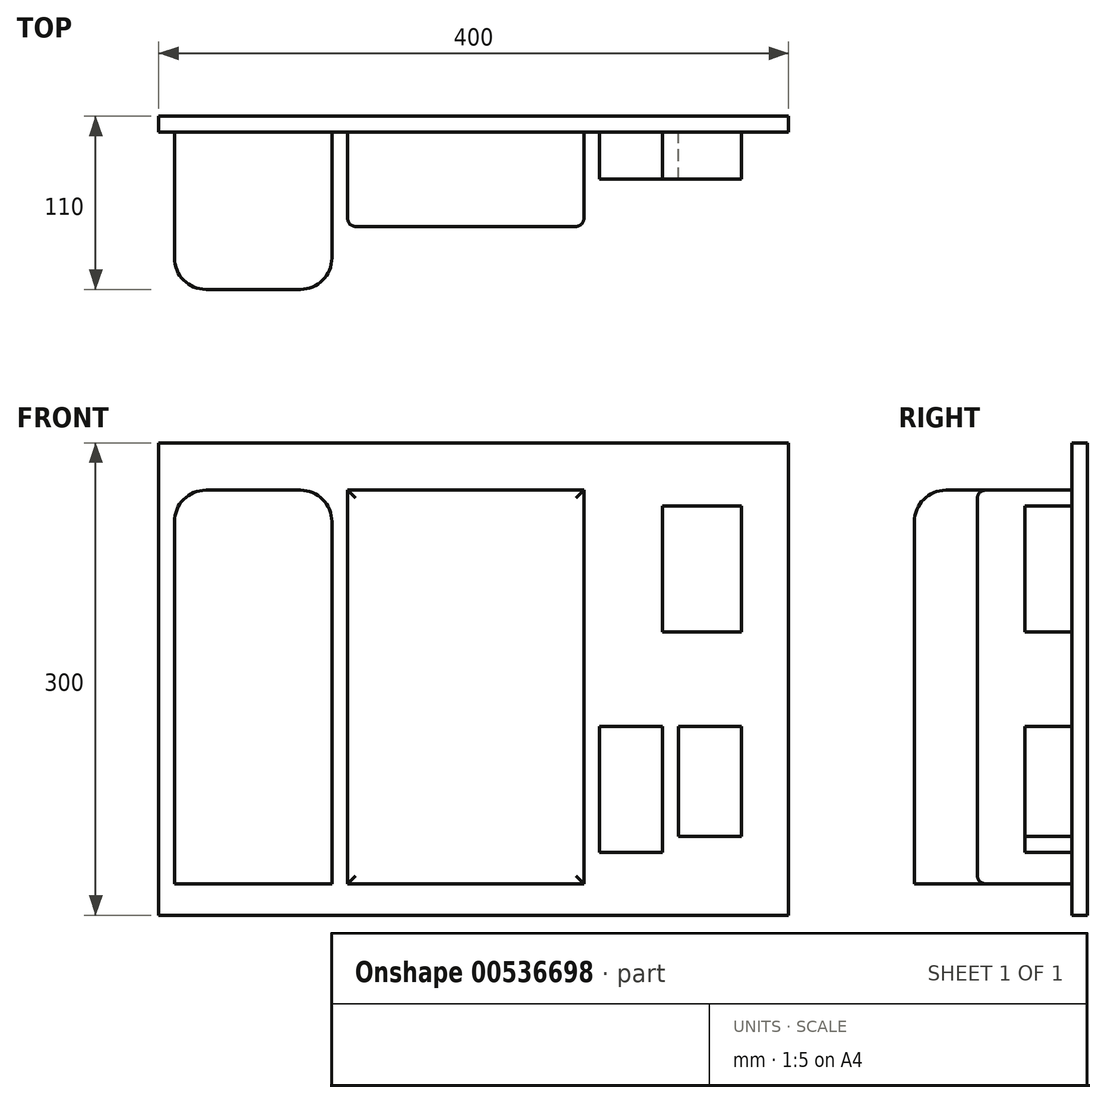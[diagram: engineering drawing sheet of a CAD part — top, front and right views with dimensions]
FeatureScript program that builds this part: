
annotation { "Feature Type Name" : "Feature", "Feature Type Description" : "" }
export const myFeature = defineFeature(function(context is Context, id is Id, definition is map)
    precondition{}
    {
        {
            var Q0;
            Q0=qCreatedBy(makeId("Front.planeOp"),FACE);
            var sketch = newSketch(context, id + "F0", { "sketchPlane" : qUnion([Q0])});
            skLineSegment(sketch, "E0.bottom", {"start": v(-200, 150) * mm, "end": v(200, 150) * mm});
            skLineSegment(sketch, "E0.top", {"start": v(-200, -150) * mm, "end": v(200, -150) * mm});
            skLineSegment(sketch, "E0.left", {"start": v(-200, 150) * mm, "end": v(-200, -150) * mm});
            skLineSegment(sketch, "E0.right", {"start": v(200, 150) * mm, "end": v(200, -150) * mm});
            skSolve(sketch);
        }
        {
            var Q0;
            Q0=makeQuery(id+"F0.imprint","IMPRINT",FACE,{"disambiguationData":[TD([[makeQuery(id+"F0.imprint","IMPRINT",EDGE,{"derivedFrom":sQuery(id+"F0.wireOp",EDGE,"E0.bottom")}),-1.0]])]});
            extrude(context, id + "F1", {"entities" : qUnion([Q0]), "endBound" : BoundingType.SYMMETRIC, "depth" : 10 * mm, "offsetDistance" : 25 * mm});
        }
        {
            var Q0;
            Q0=makeQuery(id+"F1.opExtrude","CAP_FACE",FACE,{"disambiguationData":[OSD([sQuery(id+"F0.wireOp",EDGE,"E0.bottom"),sQuery(id+"F0.wireOp",EDGE,"E0.top"),sQuery(id+"F0.wireOp",EDGE,"E0.left"),sQuery(id+"F0.wireOp",EDGE,"E0.right")])],"isStart":false});
            var sketch = newSketch(context, id + "F2", { "sketchPlane" : qUnion([Q0])});
            skLineSegment(sketch, "E1.bottom", {"start": v(-190, 120) * mm, "end": v(-90, 120) * mm});
            skLineSegment(sketch, "E1.top", {"start": v(-190, -130) * mm, "end": v(-90, -130) * mm});
            skLineSegment(sketch, "E1.left", {"start": v(-190, 120) * mm, "end": v(-190, -130) * mm});
            skLineSegment(sketch, "E1.right", {"start": v(-90, 120) * mm, "end": v(-90, -130) * mm});
            skLineSegment(sketch, "E2.bottom", {"start": v(-80, 120) * mm, "end": v(70, 120) * mm});
            skLineSegment(sketch, "E2.top", {"start": v(-80, -130) * mm, "end": v(70, -130) * mm});
            skLineSegment(sketch, "E2.left", {"start": v(-80, 120) * mm, "end": v(-80, -130) * mm});
            skLineSegment(sketch, "E2.right", {"start": v(70, 120) * mm, "end": v(70, -130) * mm});
            skLineSegment(sketch, "E3.bottom", {"start": v(120, 110) * mm, "end": v(170, 110) * mm});
            skLineSegment(sketch, "E3.top", {"start": v(120, 30) * mm, "end": v(170, 30) * mm});
            skLineSegment(sketch, "E3.left", {"start": v(120, 110) * mm, "end": v(120, 30) * mm});
            skLineSegment(sketch, "E3.right", {"start": v(170, 110) * mm, "end": v(170, 30) * mm});
            skLineSegment(sketch, "E4.bottom", {"start": v(130, -30) * mm, "end": v(170, -30) * mm});
            skLineSegment(sketch, "E4.top", {"start": v(130, -100) * mm, "end": v(170, -100) * mm});
            skLineSegment(sketch, "E4.left", {"start": v(130, -30) * mm, "end": v(130, -100) * mm});
            skLineSegment(sketch, "E4.right", {"start": v(170, -30) * mm, "end": v(170, -100) * mm});
            skLineSegment(sketch, "E5.bottom", {"start": v(80, -30) * mm, "end": v(120, -30) * mm});
            skLineSegment(sketch, "E5.top", {"start": v(80, -110) * mm, "end": v(120, -110) * mm});
            skLineSegment(sketch, "E5.left", {"start": v(80, -30) * mm, "end": v(80, -110) * mm});
            skLineSegment(sketch, "E5.right", {"start": v(120, -30) * mm, "end": v(120, -110) * mm});
            skSolve(sketch);
        }
        {
            var Q0;
            Q0=makeQuery(id+"F2.imprint","IMPRINT",FACE,{"disambiguationData":[TD([[makeQuery(id+"F2.imprint","IMPRINT",EDGE,{"derivedFrom":sQuery(id+"F2.wireOp",EDGE,"E1.bottom")}),-1.0]])]});
            extrude(context, id + "F3", {"entities" : qUnion([Q0]), "depth" : 100 * mm, "offsetDistance" : 25 * mm});
        }
        {
            var Q0;
            Q0=makeQuery(id+"F2.imprint","IMPRINT",FACE,{"disambiguationData":[TD([[makeQuery(id+"F2.imprint","IMPRINT",EDGE,{"derivedFrom":sQuery(id+"F2.wireOp",EDGE,"E2.bottom")}),-1.0]])]});
            extrude(context, id + "F4", {"entities" : qUnion([Q0]), "depth" : 60 * mm, "offsetDistance" : 25 * mm});
        }
        {
            var Q0;
            Q0=makeQuery(id+"F1.opExtrude","CAP_FACE",FACE,{"disambiguationData":[OSD([sQuery(id+"F0.wireOp",EDGE,"E0.bottom"),sQuery(id+"F0.wireOp",EDGE,"E0.top"),sQuery(id+"F0.wireOp",EDGE,"E0.left"),sQuery(id+"F0.wireOp",EDGE,"E0.right")])],"isStart":false});
            var sketch = newSketch(context, id + "F5", { "sketchPlane" : qUnion([Q0])});
            skLineSegment(sketch, "E6.0", {"start": v(-190, 120) * mm, "end": v(-90, 120) * mm});
            skLineSegment(sketch, "E6.1", {"start": v(-190, -130) * mm, "end": v(-90, -130) * mm});
            skLineSegment(sketch, "E6.2", {"start": v(-190, 120) * mm, "end": v(-190, -130) * mm});
            skLineSegment(sketch, "E6.3", {"start": v(-90, 120) * mm, "end": v(-90, -130) * mm});
            skLineSegment(sketch, "E6.4", {"start": v(-80, 120) * mm, "end": v(70, 120) * mm});
            skLineSegment(sketch, "E6.5", {"start": v(-80, -130) * mm, "end": v(70, -130) * mm});
            skLineSegment(sketch, "E6.6", {"start": v(-80, 120) * mm, "end": v(-80, -130) * mm});
            skLineSegment(sketch, "E6.7", {"start": v(70, 120) * mm, "end": v(70, -130) * mm});
            skLineSegment(sketch, "E6.8", {"start": v(120, 110) * mm, "end": v(170, 110) * mm});
            skLineSegment(sketch, "E6.9", {"start": v(120, 30) * mm, "end": v(170, 30) * mm});
            skLineSegment(sketch, "E6.10", {"start": v(120, 110) * mm, "end": v(120, 30) * mm});
            skLineSegment(sketch, "E6.11", {"start": v(170, 110) * mm, "end": v(170, 30) * mm});
            skLineSegment(sketch, "E6.12", {"start": v(130, -30) * mm, "end": v(170, -30) * mm});
            skLineSegment(sketch, "E6.13", {"start": v(130, -100) * mm, "end": v(170, -100) * mm});
            skLineSegment(sketch, "E6.14", {"start": v(130, -30) * mm, "end": v(130, -100) * mm});
            skLineSegment(sketch, "E6.15", {"start": v(170, -30) * mm, "end": v(170, -100) * mm});
            skLineSegment(sketch, "E6.16", {"start": v(80, -30) * mm, "end": v(120, -30) * mm});
            skLineSegment(sketch, "E6.17", {"start": v(80, -110) * mm, "end": v(120, -110) * mm});
            skLineSegment(sketch, "E6.18", {"start": v(80, -30) * mm, "end": v(80, -110) * mm});
            skLineSegment(sketch, "E6.19", {"start": v(120, -30) * mm, "end": v(120, -110) * mm});
            skSolve(sketch);
        }
        {
            var Q0;
            Q0=makeQuery(id+"F5.imprint","IMPRINT",FACE,{"disambiguationData":[TD([[makeQuery(id+"F5.imprint","IMPRINT",EDGE,{"derivedFrom":sQuery(id+"F5.wireOp",EDGE,"E6.8")}),-1.0]])]});
            var Q1;
            Q1=makeQuery(id+"F5.imprint","IMPRINT",FACE,{"disambiguationData":[TD([[makeQuery(id+"F5.imprint","IMPRINT",EDGE,{"derivedFrom":sQuery(id+"F5.wireOp",EDGE,"E6.12")}),-1.0]])]});
            var Q2;
            Q2=makeQuery(id+"F5.imprint","IMPRINT",FACE,{"disambiguationData":[TD([[makeQuery(id+"F5.imprint","IMPRINT",EDGE,{"derivedFrom":sQuery(id+"F5.wireOp",EDGE,"E6.16")}),-1.0]])]});
            extrude(context, id + "F6", {"entities" : qUnion([Q0, Q1, Q2]), "depth" : 30 * mm, "offsetDistance" : 25 * mm});
        }
        {
            var Q0;
            Q0=makeQuery(id+"F3.opExtrude","CAP_EDGE",EDGE,{"disambiguationData":[OSD([sQuery(id+"F2.wireOp",EDGE,"E1.left")])],"isStart":false});
            var Q1;
            Q1=makeQuery(id+"F3.opExtrude","SWEPT_EDGE",EDGE,{"disambiguationData":[OSD([sQuery(id+"F2.wireOp",EDGE,"E1.bottom"),sQuery(id+"F2.wireOp",EDGE,"E1.right")])]});
            var Q2;
            Q2=makeQuery(id+"F3.opExtrude","SWEPT_EDGE",EDGE,{"disambiguationData":[OSD([sQuery(id+"F2.wireOp",EDGE,"E1.bottom"),sQuery(id+"F2.wireOp",EDGE,"E1.left")])]});
            var Q3;
            Q3=makeQuery(id+"F3.opExtrude","CAP_EDGE",EDGE,{"disambiguationData":[OSD([sQuery(id+"F2.wireOp",EDGE,"E1.right")])],"isStart":false});
            var Q4;
            Q4=makeQuery(id+"F3.opExtrude","CAP_EDGE",EDGE,{"disambiguationData":[OSD([sQuery(id+"F2.wireOp",EDGE,"E1.bottom")])],"isStart":false});
            fillet(context, id + "F7", {"entities" : qUnion([Q0, Q1, Q2, Q3, Q4]), "radius" : 20 * mm, "tangentPropagation" : true, "allowEdgeOverflow" : false});
        }
        {
            var Q0;
            Q0=makeQuery(id+"F4.opExtrude","CAP_EDGE",EDGE,{"disambiguationData":[OSD([sQuery(id+"F2.wireOp",EDGE,"E2.bottom")])],"isStart":false});
            var Q1;
            Q1=makeQuery(id+"F4.opExtrude","CAP_EDGE",EDGE,{"disambiguationData":[OSD([sQuery(id+"F2.wireOp",EDGE,"E2.right")])],"isStart":false});
            var Q2;
            Q2=makeQuery(id+"F4.opExtrude","CAP_EDGE",EDGE,{"disambiguationData":[OSD([sQuery(id+"F2.wireOp",EDGE,"E2.left")])],"isStart":false});
            var Q3;
            Q3=makeQuery(id+"F4.opExtrude","CAP_EDGE",EDGE,{"disambiguationData":[OSD([sQuery(id+"F2.wireOp",EDGE,"E2.top")])],"isStart":false});
            fillet(context, id + "F8", {"entities" : qUnion([Q0, Q1, Q2, Q3]), "radius" : 5 * mm, "tangentPropagation" : true, "allowEdgeOverflow" : false});
        }
    });
